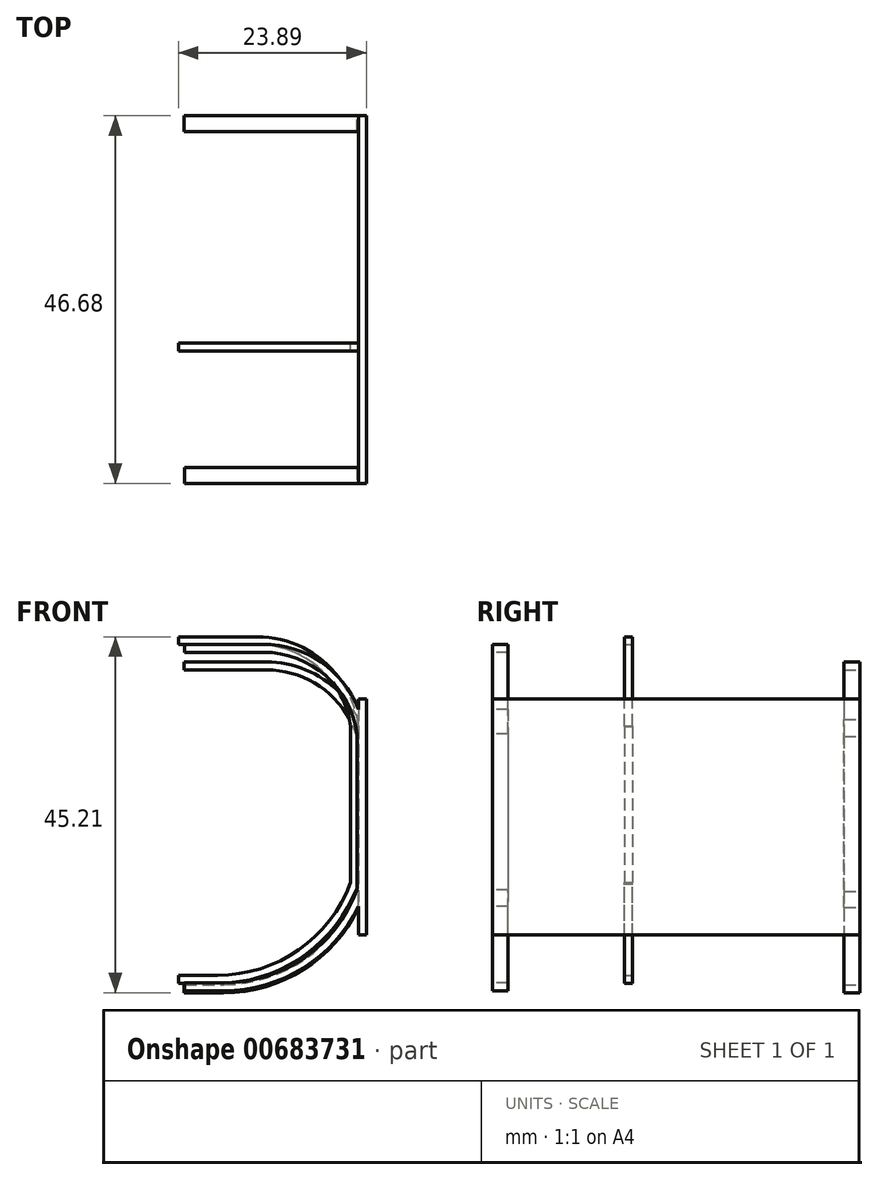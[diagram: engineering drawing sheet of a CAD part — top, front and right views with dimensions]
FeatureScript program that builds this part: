
annotation { "Feature Type Name" : "Feature", "Feature Type Description" : "" }
export const myFeature = defineFeature(function(context is Context, id is Id, definition is map)
    precondition{}
    {
        {
            var Q0;
            Q0=qCreatedBy(makeId("Front.planeOp"),FACE);
            var sketch = newSketch(context, id + "F0", { "sketchPlane" : qUnion([Q0])});
            skLineSegment(sketch, "E0", {"start": v(-63.74, 24.88) * mm, "end": v(-53.74, 24.88) * mm});
            skArc(sketch, "E1", {"start": v(-53.74, 24.88) * mm, "mid": v(-45.85, 21.91) * mm, "end": v(-41.85, 14.5) * mm});
            skLineSegment(sketch, "E2", {"start": v(-63.74, -17.12) * mm, "end": v(-58.74, -17.12) * mm});
            skArc(sketch, "E3", {"start": v(-58.74, -17.12) * mm, "mid": v(-48.44, -13.89) * mm, "end": v(-41.85, -5.34) * mm});
            skLineSegment(sketch, "E4", {"start": v(-41.85, 14.5) * mm, "end": v(-41.85, -5.34) * mm});
            skLineSegment(sketch, "E5.0", {"start": v(-63.74, -18.12) * mm, "end": v(-58.74, -18.12) * mm});
            skLineSegment(sketch, "E5.1", {"start": v(-63.74, 25.88) * mm, "end": v(-53.74, 25.88) * mm});
            skArc(sketch, "E5.2", {"start": v(-53.74, 25.88) * mm, "mid": v(-45.16, 22.65) * mm, "end": v(-40.85, 14.56) * mm});
            skLineSegment(sketch, "E5.3", {"start": v(-40.85, 14.56) * mm, "end": v(-40.85, -5.52) * mm});
            skArc(sketch, "E5.4", {"start": v(-58.74, -18.12) * mm, "mid": v(-47.8, -14.66) * mm, "end": v(-40.85, -5.52) * mm});
            skLineSegment(sketch, "E6", {"start": v(-63.74, 25.88) * mm, "end": v(-63.74, 24.88) * mm});
            skLineSegment(sketch, "E7", {"start": v(-63.74, -18.12) * mm, "end": v(-63.74, -17.12) * mm});
            skSolve(sketch);
        }
        {
            var Q0;
            Q0 = qSketchRegion(id + "F0", true);
            extrude(context, id + "F1", {"entities" : qUnion([Q0]), "depth" : 1 * mm, "offsetDistance" : 25.4 * mm});
        }
        {
            var Q0;
            Q0=makeQuery(id+"F1.opExtrude","SWEPT_FACE",FACE,{"disambiguationData":[OSD([sQuery(id+"F0.wireOp",EDGE,"E5.3")])]});
            var sketch = newSketch(context, id + "F2", { "sketchPlane" : qUnion([Q0])});
            skLineSegment(sketch, "E8.bottom", {"start": v(-17.81, 18) * mm, "end": v(28.87, 18) * mm});
            skLineSegment(sketch, "E8.top", {"start": v(-17.81, -12) * mm, "end": v(28.87, -12) * mm});
            skLineSegment(sketch, "E8.left", {"start": v(-17.81, 18) * mm, "end": v(-17.81, -12) * mm});
            skLineSegment(sketch, "E8.right", {"start": v(28.87, 18) * mm, "end": v(28.87, -12) * mm});
            skPoint(sketch, "E9.start.orphan", {"position": v(-22.12, -12) * mm});
            skSolve(sketch);
        }
        {
            var Q0;
            Q0 = qSketchRegion(id + "F2", true);
            extrude(context, id + "F3", {"entities" : qUnion([Q0]), "operationType" : NewBodyOperationType.ADD, "depth" : 1 * mm, "offsetDistance" : 25.4 * mm});
        }
        {
            var Q0;
            Q0=makeQuery(id+"F3.opExtrude","SWEPT_FACE",FACE,{"disambiguationData":[OSD([sQuery(id+"F2.wireOp",EDGE,"E8.right")])]});
            var sketch = newSketch(context, id + "F4", { "sketchPlane" : qUnion([Q0])});
            skLineSegment(sketch, "E10.MirrorCS", {"start": v(62.99, 22.67) * mm, "end": v(62.99, 21.67) * mm});
            skLineSegment(sketch, "E11.MirrorCS", {"start": v(62.99, -18.33) * mm, "end": v(62.99, -19.33) * mm});
            skLineSegment(sketch, "E12.MirrorCS", {"start": v(62.99, 21.67) * mm, "end": v(52.54, 21.67) * mm});
            skLineSegment(sketch, "E13.MirrorCS", {"start": v(62.99, 22.67) * mm, "end": v(52.54, 22.67) * mm});
            skArc(sketch, "E14.MirrorCS", {"start": v(57.99, -18.33) * mm, "mid": v(47.67, -15.07) * mm, "end": v(41.08, -6.49) * mm});
            skArc(sketch, "E15.MirrorCS", {"start": v(57.99, -19.33) * mm, "mid": v(47.02, -15.84) * mm, "end": v(40.08, -6.66) * mm});
            skLineSegment(sketch, "E16.MirrorCS", {"start": v(62.99, -18.33) * mm, "end": v(57.99, -18.33) * mm});
            skArc(sketch, "E17.MirrorCS", {"start": v(52.54, 22.67) * mm, "mid": v(44.76, 20.09) * mm, "end": v(40.08, 13.37) * mm});
            skArc(sketch, "E18.MirrorCS", {"start": v(52.54, 21.67) * mm, "mid": v(45.42, 19.33) * mm, "end": v(41.08, 13.22) * mm});
            skLineSegment(sketch, "E19.MirrorCS", {"start": v(40.08, 13.37) * mm, "end": v(40.08, -6.66) * mm});
            skLineSegment(sketch, "E20.MirrorCS", {"start": v(41.08, 13.22) * mm, "end": v(41.08, -6.49) * mm});
            skLineSegment(sketch, "E21.MirrorCS", {"start": v(62.99, -19.33) * mm, "end": v(57.99, -19.33) * mm});
            skSolve(sketch);
        }
        {
            var Q0;
            Q0 = qSketchRegion(id + "F4", true);
            extrude(context, id + "F5", {"entities" : qUnion([Q0]), "operationType" : NewBodyOperationType.ADD, "oppositeDirection" : true, "depth" : 2 * mm, "offsetDistance" : 25.4 * mm});
        }
        {
            var Q0;
            Q0=makeQuery(id+"F3.opExtrude","SWEPT_FACE",FACE,{"disambiguationData":[OSD([sQuery(id+"F2.wireOp",EDGE,"E8.left")])]});
            var sketch = newSketch(context, id + "F6", { "sketchPlane" : qUnion([Q0])});
            skLineSegment(sketch, "E22", {"start": v(-62.94, 23.92) * mm, "end": v(-52.94, 23.92) * mm});
            skArc(sketch, "E23", {"start": v(-52.94, 23.92) * mm, "mid": v(-45.05, 20.96) * mm, "end": v(-41.05, 13.53) * mm});
            skLineSegment(sketch, "E24", {"start": v(-62.94, -18.08) * mm, "end": v(-57.94, -18.08) * mm});
            skArc(sketch, "E25", {"start": v(-57.94, -18.08) * mm, "mid": v(-47.65, -14.85) * mm, "end": v(-41.05, -6.3) * mm});
            skLineSegment(sketch, "E26", {"start": v(-41.05, 13.53) * mm, "end": v(-41.05, -6.3) * mm});
            skLineSegment(sketch, "E27.0", {"start": v(-62.94, -19.08) * mm, "end": v(-57.94, -19.08) * mm});
            skLineSegment(sketch, "E27.1", {"start": v(-62.94, 24.92) * mm, "end": v(-52.94, 24.92) * mm});
            skArc(sketch, "E27.2", {"start": v(-52.94, 24.92) * mm, "mid": v(-44.37, 21.69) * mm, "end": v(-40.05, 13.6) * mm});
            skLineSegment(sketch, "E27.3", {"start": v(-40.05, 13.6) * mm, "end": v(-40.05, -6.48) * mm});
            skArc(sketch, "E27.4", {"start": v(-57.94, -19.08) * mm, "mid": v(-47, -15.62) * mm, "end": v(-40.05, -6.48) * mm});
            skLineSegment(sketch, "E28", {"start": v(-62.94, 24.92) * mm, "end": v(-62.94, 23.92) * mm});
            skLineSegment(sketch, "E29", {"start": v(-62.94, -19.08) * mm, "end": v(-62.94, -18.08) * mm});
            skSolve(sketch);
        }
        {
            var Q0;
            Q0 = qSketchRegion(id + "F6", true);
            extrude(context, id + "F7", {"entities" : qUnion([Q0]), "operationType" : NewBodyOperationType.ADD, "oppositeDirection" : true, "depth" : 2 * mm, "offsetDistance" : 25.4 * mm});
        }
    });
